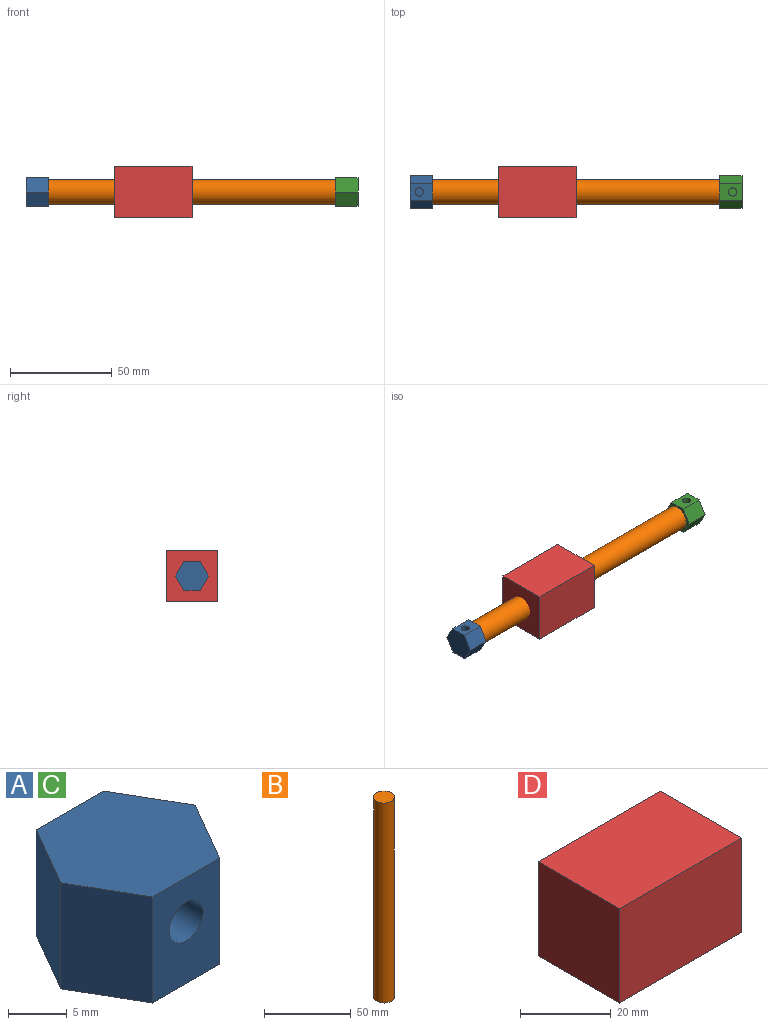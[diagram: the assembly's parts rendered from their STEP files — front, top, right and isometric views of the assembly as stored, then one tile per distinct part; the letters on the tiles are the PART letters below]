
ASSEMBLY  parts=4 mates=3
PART A: 10 faces, bbox 16.2x14x11 mm
  f0: plane 11.05x7.01mm, normal (0.87,0.5,0), area 89.4mm2, adj f1,f5,f6,f7
  f1: plane 11.05x8.1mm, normal (0,1,0), area 89.4mm2, adj f0,f2,f6,f7
  f2: plane 11.05x7.01mm, normal (-0.87,0.5,0), area 89.4mm2, adj f1,f3,f6,f7
  f3: plane 11.05x7.01mm, normal (-0.87,-0.5,0), area 89.4mm2, adj f2,f4,f6,f7
  f4: plane 11.05x8.1mm, normal (0,-1,0), area 76.5mm2, adj f3,f5,f6,f7,f8
  f5: plane 11.05x7.01mm, normal (0.87,-0.5,0), area 89.4mm2, adj f0,f4,f6,f7
  f6: plane 16.19x14.02mm, normal (0,0,1), area 170.2mm2, adj f0,f1,f2,f3,f4,f5
  f7: plane 16.19x14.02mm, normal (0,0,-1), area 170.2mm2, adj f0,f1,f2,f3,f4,f5
  f8: cylinder r=2.03mm len=9.04mm, axis (0,-1,0), area 115.4mm2, adj f4,f9
  f9: plane 4.06x4.06mm, normal (0,-1,0), area 13mm2, adj f8
PART B: 3 faces, bbox 12.1x12.1x141.2 mm
  f0: cylinder r=6.03mm len=141.22mm, axis (0,0,-1), area 5352.9mm2, adj f1,f2
  f1: plane 12.07x12.07mm, normal (0,0,1), area 114.3mm2, adj f0
  f2: plane 12.07x12.07mm, normal (0,0,-1), area 114.3mm2, adj f0
PART C: same geometry as A
PART D: 6 faces, bbox 38.1x25.4x25.4 mm
  f0: plane 25.4x25.4mm, normal (1,0,0), area 645.2mm2, adj f1,f3,f4,f5
  f1: plane 38.1x25.4mm, normal (0,1,0), area 967.7mm2, adj f0,f2,f4,f5
  f2: plane 25.4x25.4mm, normal (-1,0,0), area 645.2mm2, adj f1,f3,f4,f5
  f3: plane 38.1x25.4mm, normal (0,-1,0), area 967.7mm2, adj f0,f2,f4,f5
  f4: plane 38.1x25.4mm, normal (0,0,1), area 967.7mm2, adj f0,f1,f2,f3
  f5: plane 38.1x25.4mm, normal (0,0,-1), area 967.7mm2, adj f0,f1,f2,f3
PLACE A rot(axis=(-0.58,-0.58,0.58),120deg) t=(-51.56,0,12.7)mm
PLACE B rot(axis=(0,-1,0),90deg) t=(89.66,0,12.7)mm
PLACE C rot(axis=(-0.58,0.58,-0.58),120deg) t=(89.66,0,12.7)mm
PLACE D at identity fixed
MATE fastened A.f7 <-> B.f0  axis (1,0,0) through (-51.56,0,12.7)mm
MATE fastened C.f7 <-> B.f0  axis (-1,0,0) through (89.66,0,12.7)mm
MATE fastened B.f0 <-> D.f0  axis (1,0,0) through (19.05,0,12.7)mm
